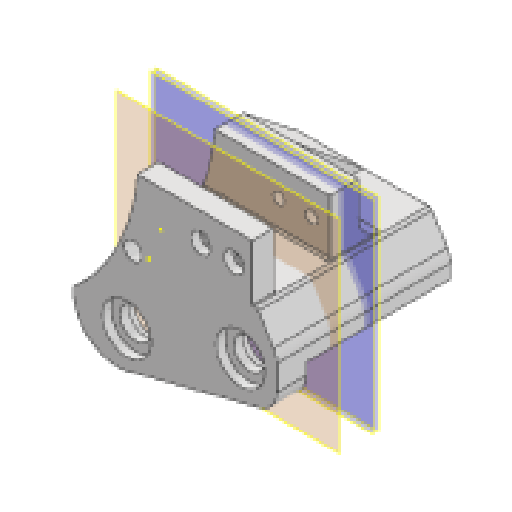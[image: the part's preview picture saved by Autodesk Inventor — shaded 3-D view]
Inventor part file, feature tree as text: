
AUTODESK INVENTOR PART (.ipt)
format: ipt  version: 2025 (Build 290162000, 162)  size: 850,944 bytes
history: native  units: in
note: dims shown in document units (in); Inventor stores cm internally (conversion verified against a paired STEP export)
features: sketch x51, extrude x49, projected_geometry x46, fillet x15, mirror x6, plane x5, reference x3, other x3, thicken_offset x1, chamfer x1, pattern_linear x1
ambient origin geometry x8: Origin, YZ Plane, XZ Plane, XY Plane, X Axis, Y Axis, Z Axis, Center Point
bodies: Solid1 (feature_tree)
feature tree (181):
  extrude  "Extrusion1"  Depth=0.25in
  extrude  "Extrusion2"  Depth=0.5512in
  extrude  "Extrusion7"  Depth=0.874in
  extrude  "Extrusion10"  Depth=0.2165in TaperAngle=0.0deg
  extrude  "Extrusion11"  Depth=0.315in
  extrude  "Extrusion12"  TaperAngle=0.0deg  [1 undecoded]
  extrude  "Extrusion13"  Depth=0.3937in TaperAngle=0.0deg
  mirror  "Mirror1"
  fillet  "Fillet5"  Radius=0.3937in
  extrude  "Extrusion14"  Depth=0.3937in
  fillet  "Fillet6"  [1 undecoded]
  extrude  "Extrusion15"  Depth=0.3937in
  thicken_offset  "Thicken1"
  fillet  "Fillet7"  Radius=0.3858in
  extrude  "Extrusion16"  Depth=0.5118in
  extrude  "Extrusion17"  Depth=1.0in
  fillet  "Fillet8"  Radius=1.0in
  extrude  "Extrusion18"  Depth=0.3937in
  extrude  "Extrusion19"  Depth=1.0in TaperAngle=0.0deg
  extrude  "Extrusion20"  Depth=0.315in
  extrude  "Extrusion21"  Depth=0.3228in
  extrude  "Extrusion22"  Depth=0.2756in
  extrude  "Extrusion23"  Depth=0.2047in
  plane  "Work Plane1"
  mirror  "Mirror2"
  fillet  "Fillet9"  Radius=0.2047in
  fillet  "Fillet10"  [1 undecoded]
  extrude  "Extrusion24"  Depth=0.3543in
  extrude  "Extrusion25"  Depth=0.7874in
  fillet  "Fillet12"  Radius=0.1969in
  fillet  "Fillet13"  Radius=0.1969in
  chamfer  "Chamfer2"  [1 undecoded]
  extrude  "Extrusion26"  Depth=0.5in
  sketch  "Sketch27"  dims[d97=0.1181in d98=0.0787in d99=45.0deg d100=0.3937in d101=0.0in]
  extrude  "Extrusion27"  Depth=0.3937in TaperAngle=0.0deg
  extrude  "Extrusion28"  Depth=0.3937in TaperAngle=0.0deg
  extrude  "Extrusion29"  Depth=0.7874in
  pattern_linear  "Rectangular Pattern1"  Count1=2  [1 undecoded]
  extrude  "Extrusion30"  Depth=0.3937in TaperAngle=0.0deg
  extrude  "Extrusion31"  Depth=0.3937in TaperAngle=0.0deg
  extrude  "Extrusion32"  Depth=0.3937in TaperAngle=0.0deg
  fillet  "Fillet14"  Radius=0.3937in
  extrude  "Extrusion33"  TaperAngle=0.0deg  [1 undecoded]
  extrude  "Extrusion34"  Depth=0.8268in
  fillet  "Fillet15"  Radius=0.3937in
  sketch  "Sketch39"  dims[d136=0.3937in d137=0.0in d141=0.3937in d142=0.0in]
  extrude  "Extrusion39"  Depth=0.2756in TaperAngle=0.0deg
  extrude  "Extrusion40"  Depth=0.0787in TaperAngle=0.0deg
  extrude  "Extrusion44"  Depth=0.0787in
  extrude  "Extrusion41"  Depth=0.3937in
  extrude  "Extrusion42"  Depth=0.7874in
  extrude  "Extrusion43"  Depth=0.3937in TaperAngle=0.0deg
  plane  "Work Plane2"
  mirror  "Mirror3"
  extrude  "Extrusion45"  Depth=0.3937in
  extrude  "Extrusion46"  TaperAngle=0.0deg  [1 undecoded]
  extrude  "Extrusion47"  Depth=0.8268in TaperAngle=0.0deg
  plane  "Work Plane3"
  mirror  "Mirror4"
  plane  "Work Plane4"
  mirror  "Mirror5"
  sketch  "Sketch51"  dims[d183=0.5906in d184=0.0in d185=0.3937in d186=0.0in]
  extrude  "Extrusion49"  Depth=0.3937in TaperAngle=0.0deg
  plane  "Work Plane5"
  mirror  "Mirror6"
  extrude  "Extrusion50"  Depth=0.0344in
  extrude  "Extrusion51"  TaperAngle=0.0deg  [1 undecoded]
  fillet  "Fillet21"  [1 undecoded]
  fillet  "Fillet22"  [1 undecoded]
  fillet  "Fillet23"  [1 undecoded]
  fillet  "Fillet24"  [1 undecoded]
  fillet  "Fillet26"  [1 undecoded]
  extrude  "Extrusion52"  TaperAngle=0.0deg  [1 undecoded]
  extrude  "Extrusion53"  [1 undecoded]
  extrude  "Extrusion54"  [1 undecoded]
  extrude  "Extrusion55"  [1 undecoded]
  extrude  "Extrusion57"  [1 undecoded]
  extrude  "Extrusion58"  [1 undecoded]
  extrude  "Extrusion59"  [1 undecoded]
  extrude  "Extrusion60"  [1 undecoded]
  extrude  "Extrusion61"  [1 undecoded]
  sketch  "Sketch1"  dims[d1=1.005in d2=0.25in]
  sketch  "Sketch2"  dims[d3=2.0in d4=0.0in d5=0.5512in]
  projected_geometry  "Projected Loop1"
  sketch  "Sketch7"  dims[d6=0.0in d7=0.0in d21=0.874in]
  sketch  "Sketch10"  dims[d22=0.1575in d23=0.0in d32=0.2165in d33=0.0in]
  projected_geometry  "Projected Loop7"
  sketch  "Sketch11"  dims[d34=1.1024in d35=0.315in]
  sketch  "Sketch12"  dims[d36=0.2047in d37=0.0in d38=0.0in]
  projected_geometry  "Projected Loop8"
  sketch  "Sketch13"  dims[d39=0.3937in d40=0.0in d42=1.0236in d43=0.0in d45=0.3937in]
  projected_geometry  "Projected Loop9"
  sketch  "Sketch14"  dims[d46=1.0236in d47=0.0in d48=0.3937in d49=0.0in d50=0.0in]
  projected_geometry  "Projected Loop10"
  sketch  "Sketch15"  dims[d51=0.0591in d52=0.1in d53=0.3937in d54=0.3858in]
  projected_geometry  "Projected Loop11"
  sketch  "Sketch16"  dims[d55=0.0079in d56=0.5118in]
  projected_geometry  "Projected Loop12"
  reference  "Reference1"
  sketch  "Sketch17"  dims[d57=0.2756in d58=0.1969in d59=1.0in d60=0.0in]
  projected_geometry  "Projected Loop13"
  sketch  "Sketch18"  dims[d61=1.0in d62=0.0in d63=0.3937in]
  projected_geometry  "Projected Loop14"
  reference  "Reference2"
  sketch  "Sketch19"  dims[d64=0.2047in d65=1.0in d66=0.0in]
  sketch  "Sketch20"  dims[d67=0.315in d68=0.315in]
  sketch  "Sketch21"  dims[d69=0.1969in d70=0.0in d71=0.3228in]
  sketch  "Sketch22"  dims[d72=0.315in d73=0.0in d74=0.2756in]
  reference  "Reference3"
  sketch  "Sketch23"  dims[d75=0.4724in d76=0.0in d77=0.2047in d78=0.2047in d79=0.0in d80=0.0in]
  projected_geometry  "Projected Loop15"
  sketch  "Sketch24"  dims[d81=0.3543in d82=0.3543in]
  projected_geometry  "Projected Loop16"
  projected_geometry  "Projected Loop17"
  sketch  "Sketch25"  dims[d83=0.315in d84=0.0in d85=0.7874in d86=0.1969in d88=0.1969in d89=0.0in d90=0.0in d91=0.0in]
  projected_geometry  "Projected Loop18"
  sketch  "Sketch26"  dims[d92=0.5in d93=0.5in]
  projected_geometry  "Projected Loop19"
  sketch  "Sketch28"  dims[d102=0.3937in d103=0.0in d104=0.3937in d105=0.0in]
  projected_geometry  "Projected Loop20"
  projected_geometry  "Projected Loop21"
  sketch  "Sketch29"  dims[d106=0.7874in d107=0.0in d108=1.1811in d110=0.2953in]
  projected_geometry  "Projected Loop22"
  sketch  "Sketch30"  dims[d111=0.0in d112=0.0in]
  projected_geometry  "Projected Loop23"
  sketch  "Sketch31"  dims[d113=0.3937in d114=0.0in]
  sketch  "Sketch32"  dims[d115=0.3937in d116=0.0in]
  projected_geometry  "Projected Loop24"
  sketch  "Sketch33"  dims[d117=0.0394in]
  projected_geometry  "Projected Loop25"
  projected_geometry  "Projected Loop26"
  projected_geometry  "Projected Loop27"
  sketch  "Sketch34"  dims[d118=0.3937in d119=0.0in]
  projected_geometry  "Projected Loop28"
  sketch  "Sketch35"  dims[d120=0.3937in d121=0.0in d124=0.7874in]
  projected_geometry  "Projected Loop29"
  sketch  "Sketch41"  dims[d143=0.874in d146=0.3937in d147=0.0in]
  sketch  "Sketch42"  dims[d148=0.5512in d149=0.3937in d150=0.0in d151=0.3937in d152=0.0in]
  projected_geometry  "Projected Loop32"
  projected_geometry  "Projected Loop33"
  sketch  "Sketch43"  dims[d153=0.7874in d154=0.0in d155=0.0in d156=0.0in]
  projected_geometry  "Projected Loop34"
  sketch  "Sketch44"  dims[d160=0.0in d161=0.0in d162=0.8268in d164=0.3937in]
  projected_geometry  "Projected Loop35"
  sketch  "Sketch45"  dims[d165=0.3228in d166=0.2756in d167=0.0in]
  sketch  "Sketch46"  dims[d170=0.8268in d171=0.0in d172=0.0787in d173=0.0in]
  projected_geometry  "Projected Loop36"
  projected_geometry  "Projected Loop37"
  sketch  "Sketch47"  dims[d174=0.5906in d175=0.0in d176=0.0787in]
  projected_geometry  "Projected Loop38"
  sketch  "Sketch49"  dims[d177=0.3937in d178=0.3937in]
  projected_geometry  "Projected Loop40"
  sketch  "Sketch50"  dims[d179=1.5748in d181=0.7874in]
  projected_geometry  "Projected Loop41"
  sketch  "Sketch52"  dims[d187=0.3937in d188=0.0in d189=2.2815in]
  projected_geometry  "Projected Loop42"
  projected_geometry  "Projected Loop43"
  sketch  "Sketch53"  dims[d190=1.244in d191=0.0in d192=0.0in]
  projected_geometry  "Projected Loop44"
  projected_geometry  "Projected Loop45"
  projected_geometry  "Projected Loop46"
  sketch  "Sketch54"  dims[d195=0.1575in d196=0.0in d197=0.8268in d198=0.0in]
  projected_geometry  "Projected Loop47"
  sketch  "Sketch55"  dims[d199=0.3937in d200=0.0in d201=0.3937in d202=0.0in]
  projected_geometry  "Projected Loop48"
  sketch  "Sketch56"  dims[d203=0.0in d204=0.0in d24=0.0344in]
  projected_geometry  "Projected Loop49"
  sketch  "Sketch57"  dims[d27=0.0in d28=0.0in d29=0.0in d30=0.0in d87=0.0in d131=0.0in d132=0.0in]
  sketch  "Sketch58"  dims[d133=0.0in d134=0.0in]
  projected_geometry  "Projected Loop50"
  sketch  "Sketch59"  dims[d180=0.0in]
  projected_geometry  "Projected Loop51"
  sketch  "Sketch60"
  sketch  "Sketch61"
  projected_geometry  "Projected Loop52"
  sketch  "Sketch62"
  projected_geometry  "Projected Loop53"
  projected_geometry  "Projected Loop54"
  other  "<userpath>\Desktop\puppycat\woodhouseMK1.iam"
  other  "woodhouseMK1.iam"
  other  "trackBase:1"
note: 22 required parameter values undecoded (feature->parameter linkage not recoverable at this tier; creation-order binding heuristic only, values carry confidence <= 0.55)
